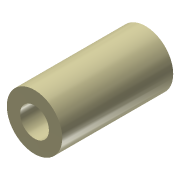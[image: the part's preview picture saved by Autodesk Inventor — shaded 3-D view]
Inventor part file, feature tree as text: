
AUTODESK INVENTOR PART (.ipt)
format: ipt  version: 2013 (Build 170138000, 138)  size: 79,872 bytes
history: native  units: in
note: dims shown in document units (in); Inventor stores cm internally (conversion verified against a paired STEP export)
features: extrude x1, sketch x1
ambient origin geometry x8: Origin, YZ Plane, XZ Plane, XY Plane, X Axis, Y Axis, Z Axis, Center Point
bodies: Solid1 (feature_tree)
feature tree (2):
  extrude  "Extrusion1"  Depth=0.5in
  sketch  "Sketch1"  dims[d0=0.26in d1=0.5in d2=1.0in d3=0.0in]
